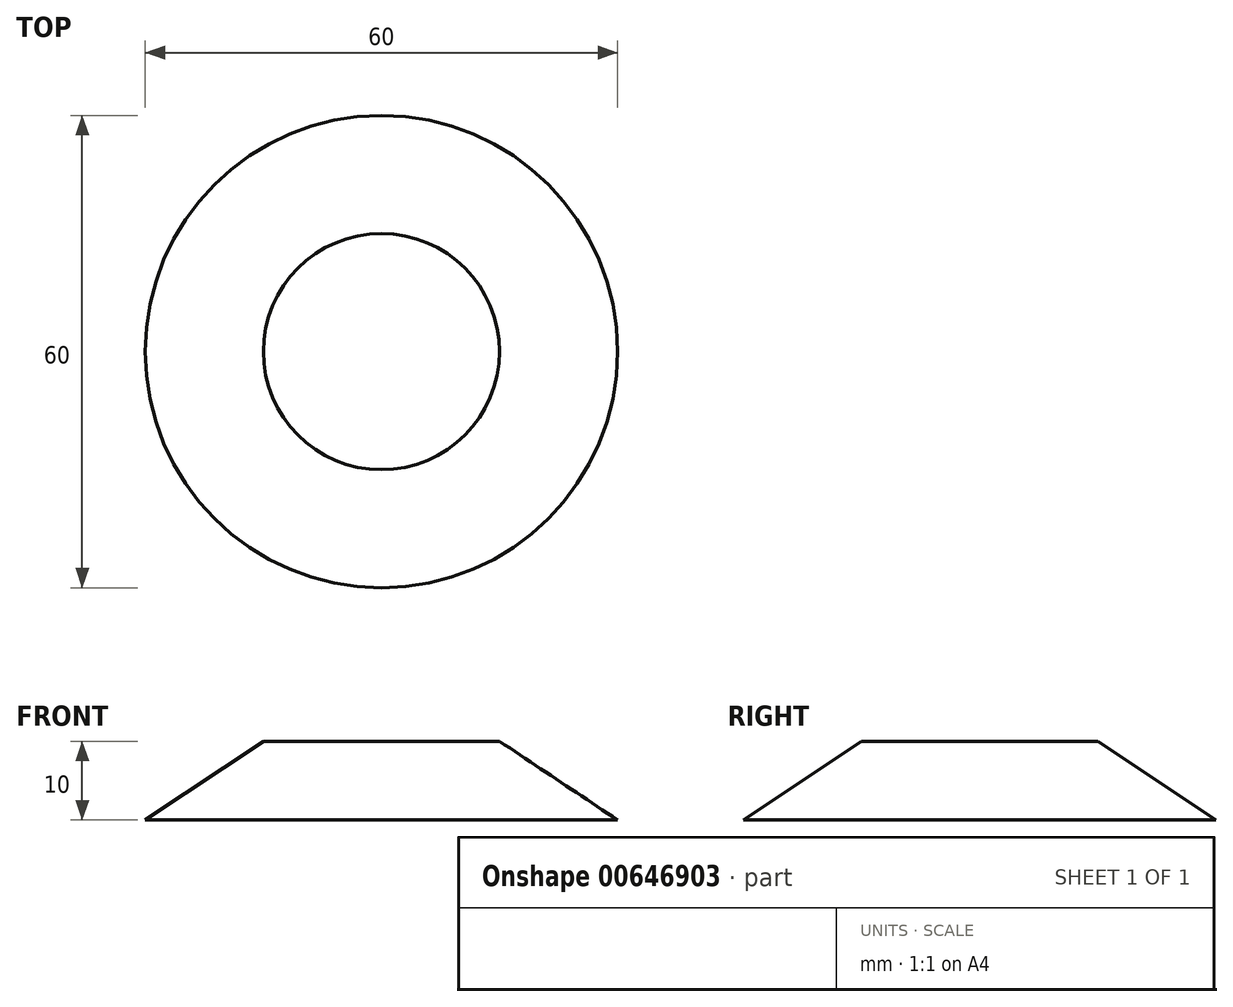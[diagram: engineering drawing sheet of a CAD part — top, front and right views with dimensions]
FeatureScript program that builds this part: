
annotation { "Feature Type Name" : "Feature", "Feature Type Description" : "" }
export const myFeature = defineFeature(function(context is Context, id is Id, definition is map)
    precondition{}
    {
        {
            var Q0;
            Q0=qCreatedBy(makeId("Right.planeOp"),FACE);
            var sketch = newSketch(context, id + "F0", { "sketchPlane" : qUnion([Q0])});
            skLineSegment(sketch, "E0", {"start": v(37.43, 10) * mm, "end": v(37.43, 0) * mm});
            skLineSegment(sketch, "E1", {"start": v(37.43, 0) * mm, "end": v(7.43, 0) * mm});
            skLineSegment(sketch, "E2", {"start": v(7.43, 0) * mm, "end": v(22.43, 10) * mm});
            skLineSegment(sketch, "E3", {"start": v(37.43, 10) * mm, "end": v(22.43, 10) * mm});
            skSolve(sketch);
        }
        {
            var Q0;
            Q0=makeQuery(id+"F0.imprint","IMPRINT",FACE,{"disambiguationData":[TD([[makeQuery(id+"F0.imprint","IMPRINT",EDGE,{"derivedFrom":sQuery(id+"F0.wireOp",EDGE,"E0")}),-1.0]])]});
            var Q1;
            Q1=sQuery(id+"F0.wireOp",EDGE,"E0");
            revolve(context, id + "F1", {"surfaceOperationType" : NewSurfaceOperationType.NEW, "entities" : qUnion([Q0]), "axis" : qUnion([Q1]), "revolveType" : RevolveType.FULL});
        }
    });
